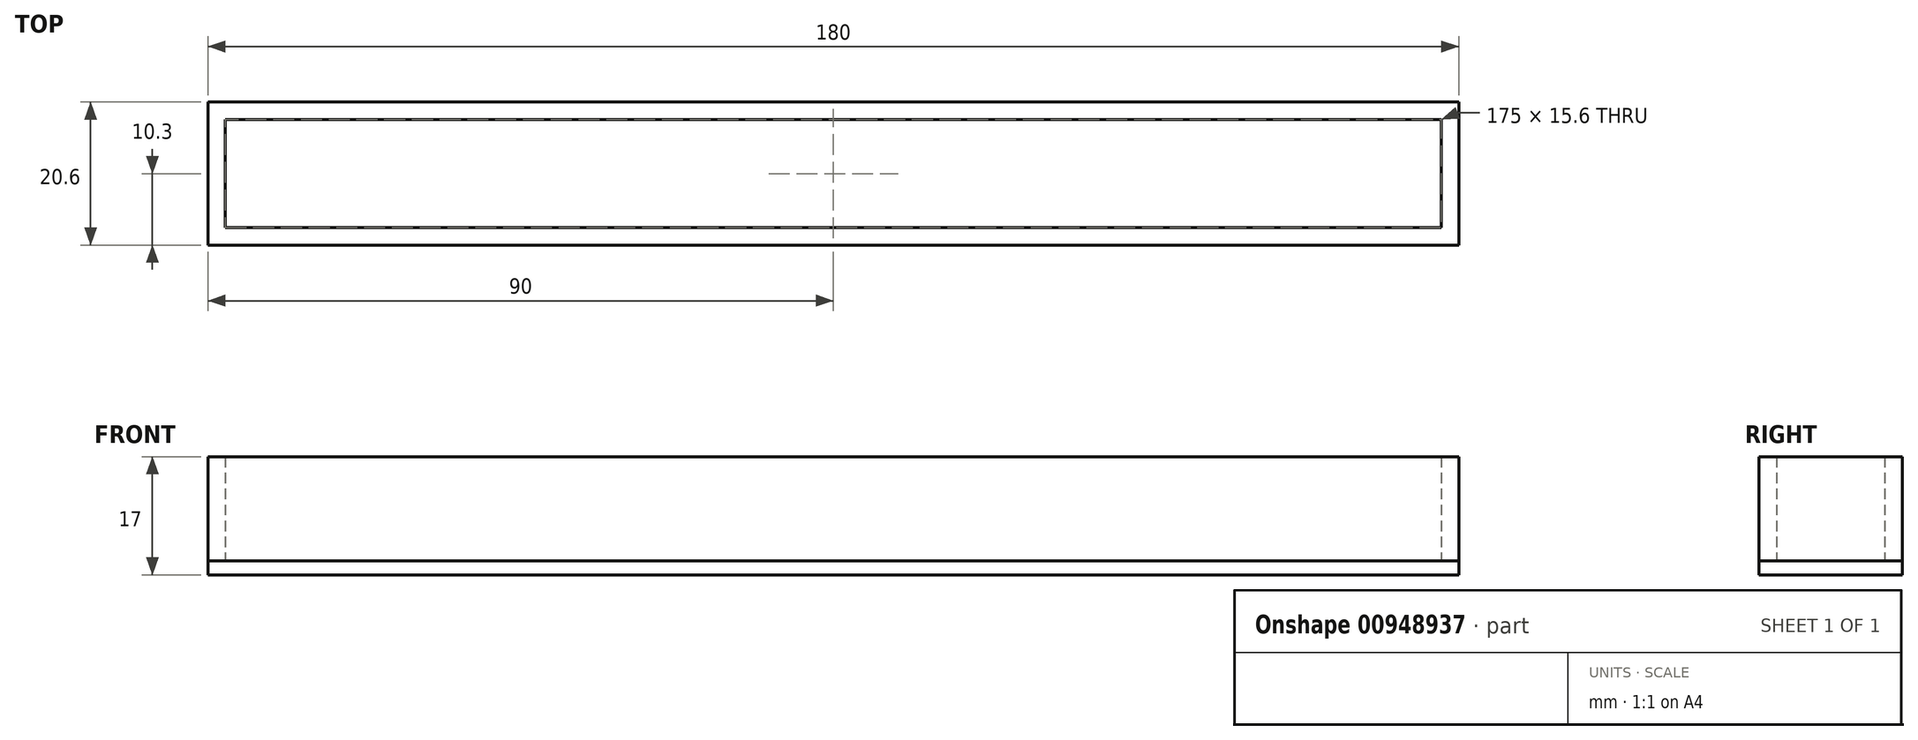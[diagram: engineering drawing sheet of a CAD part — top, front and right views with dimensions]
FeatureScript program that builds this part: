
annotation { "Feature Type Name" : "Feature", "Feature Type Description" : "" }
export const myFeature = defineFeature(function(context is Context, id is Id, definition is map)
    precondition{}
    {
        {
            var Q0;
            Q0=qCreatedBy(makeId("Top.planeOp"),FACE);
            var sketch = newSketch(context, id + "F0", { "sketchPlane" : qUnion([Q0])});
            skLineSegment(sketch, "E0.bottom", {"start": v(87.5, -7.8) * mm, "end": v(-87.5, -7.8) * mm});
            skLineSegment(sketch, "E0.top", {"start": v(87.5, 7.8) * mm, "end": v(-87.5, 7.8) * mm});
            skLineSegment(sketch, "E0.left", {"start": v(87.5, -7.8) * mm, "end": v(87.5, 7.8) * mm});
            skLineSegment(sketch, "E0.right", {"start": v(-87.5, -7.8) * mm, "end": v(-87.5, 7.8) * mm});
            skPoint(sketch, "E0.middle", {"position": v(0, 0) * mm});
            skLineSegment(sketch, "E1.bottom", {"start": v(90, -10.3) * mm, "end": v(-90, -10.3) * mm});
            skLineSegment(sketch, "E1.top", {"start": v(90, 10.3) * mm, "end": v(-90, 10.3) * mm});
            skLineSegment(sketch, "E1.left", {"start": v(90, -10.3) * mm, "end": v(90, 10.3) * mm});
            skLineSegment(sketch, "E1.right", {"start": v(-90, -10.3) * mm, "end": v(-90, 10.3) * mm});
            skSolve(sketch);
        }
        {
            var Q0;
            Q0=makeQuery(id+"F0.imprint","IMPRINT",FACE,{"disambiguationData":[TD([[makeQuery(id+"F0.imprint","IMPRINT",EDGE,{"derivedFrom":sQuery(id+"F0.wireOp",EDGE,"E0.bottom")}),1.0]])]});
            var Q1;
            Q1=makeQuery(id+"F0.imprint","IMPRINT",FACE,{"disambiguationData":[TD([[makeQuery(id+"F0.imprint","IMPRINT",EDGE,{"derivedFrom":sQuery(id+"F0.wireOp",EDGE,"E0.bottom")}),-1.0]])]});
            extrude(context, id + "F1", {"entities" : qUnion([Q0, Q1]), "oppositeDirection" : true, "depth" : 2 * mm, "offsetDistance" : 25 * mm});
        }
        {
            var Q0;
            Q0=makeQuery(id+"F0.imprint","IMPRINT",FACE,{"disambiguationData":[TD([[makeQuery(id+"F0.imprint","IMPRINT",EDGE,{"derivedFrom":sQuery(id+"F0.wireOp",EDGE,"E0.bottom")}),1.0]])]});
            var Q1;
            Q1=sQuery(id+"F0.wireOp",EDGE,"E1.right");
            var Q2;
            Q2=sQuery(id+"F0.wireOp",EDGE,"E1.top");
            var Q3;
            Q3=sQuery(id+"F0.wireOp",EDGE,"E0.top");
            var Q4;
            Q4=sQuery(id+"F0.wireOp",EDGE,"E0.right");
            var Q5;
            Q5=sQuery(id+"F0.wireOp",EDGE,"E0.bottom");
            var Q6;
            Q6=sQuery(id+"F0.wireOp",EDGE,"E1.bottom");
            var Q7;
            Q7=sQuery(id+"F0.wireOp",EDGE,"E0.left");
            var Q8;
            Q8=sQuery(id+"F0.wireOp",EDGE,"E1.left");
            extrude(context, id + "F2", {"entities" : qUnion([Q0]), "surfaceEntities" : qUnion([Q1, Q2, Q3, Q4, Q5, Q6, Q7, Q8]), "depth" : 15 * mm, "offsetDistance" : 25 * mm});
        }
    });
